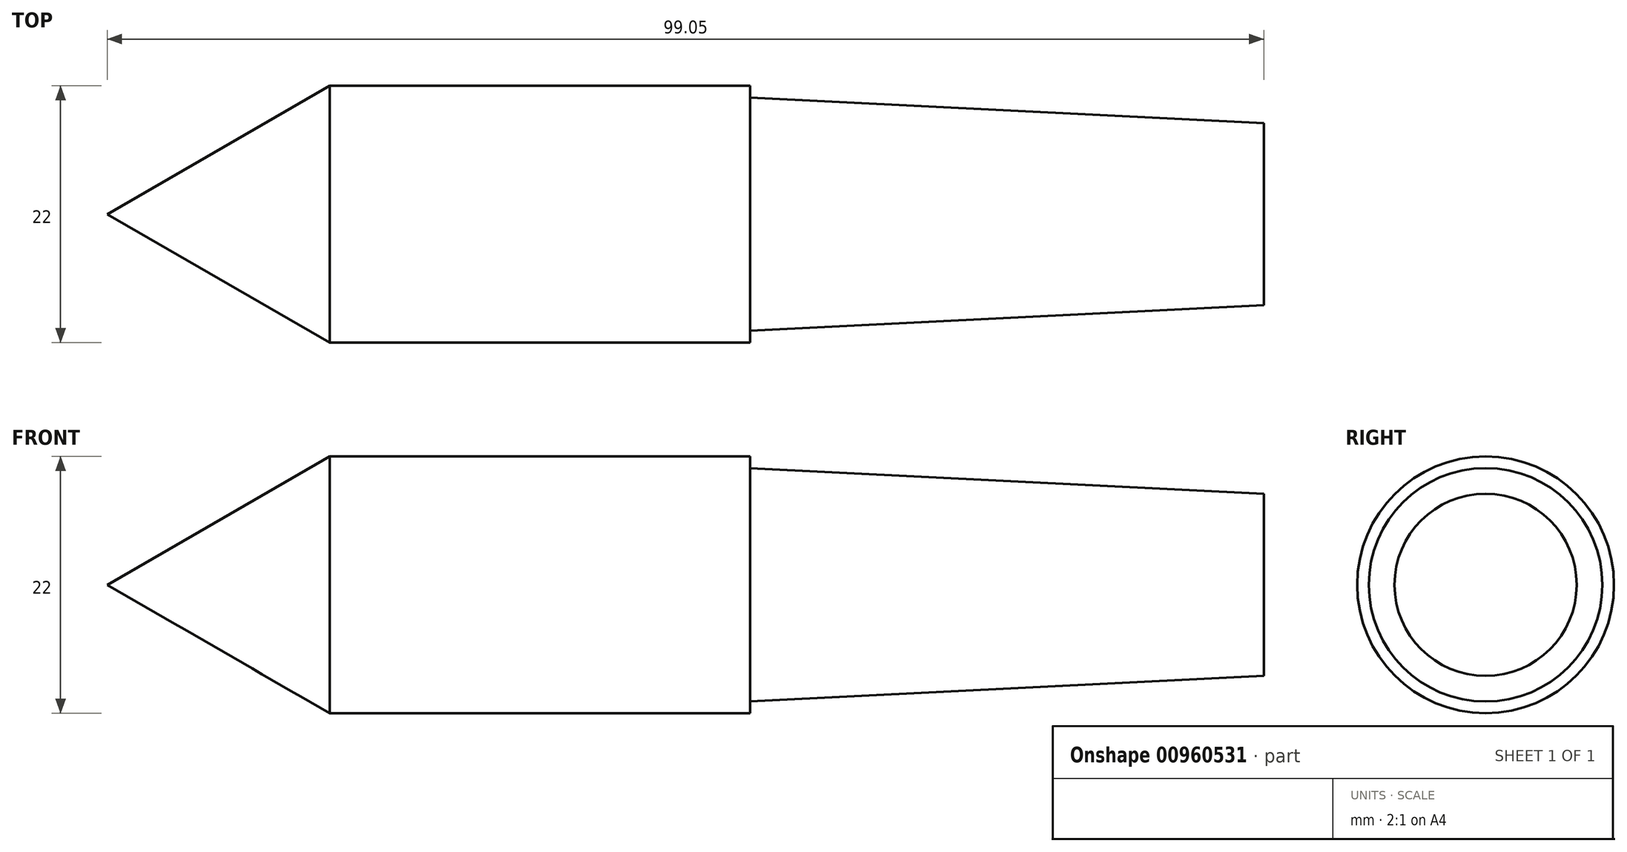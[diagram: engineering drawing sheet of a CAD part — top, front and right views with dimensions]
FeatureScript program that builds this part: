
annotation { "Feature Type Name" : "Feature", "Feature Type Description" : "" }
export const myFeature = defineFeature(function(context is Context, id is Id, definition is map)
    precondition{}
    {
        {
            var Q0;
            Q0=qCreatedBy(makeId("Front.planeOp"),FACE);
            var sketch = newSketch(context, id + "F0", { "sketchPlane" : qUnion([Q0])});
            skLineSegment(sketch, "E0", {"start": v(-55.05, 0) * mm, "end": v(-36, 11) * mm});
            skLineSegment(sketch, "E1", {"start": v(-36, 11) * mm, "end": v(0, 11) * mm});
            skLineSegment(sketch, "E2", {"start": v(0, 11) * mm, "end": v(0, 10) * mm});
            skLineSegment(sketch, "E3", {"start": v(0, 10) * mm, "end": v(44, 7.8) * mm});
            skLineSegment(sketch, "E4", {"start": v(44, 7.8) * mm, "end": v(44, 0) * mm});
            skLineSegment(sketch, "E5", {"start": v(44, 0) * mm, "end": v(-55.05, 0) * mm});
            skLineSegment(sketch, "E6", {"start": v(40, 8) * mm, "end": v(40, 0) * mm, "construction": true});
            skSolve(sketch);
        }
        {
            var Q0;
            Q0=makeQuery(id+"F0.imprint","IMPRINT",FACE,{"disambiguationData":[TD([[makeQuery(id+"F0.imprint","IMPRINT",EDGE,{"derivedFrom":sQuery(id+"F0.wireOp",EDGE,"E0")}),-1.0]])]});
            var Q1;
            Q1=sQuery(id+"F0.wireOp",EDGE,"E5");
            revolve(context, id + "F1", {"surfaceOperationType" : NewSurfaceOperationType.NEW, "entities" : qUnion([Q0]), "axis" : qUnion([Q1]), "revolveType" : RevolveType.FULL});
        }
    });
